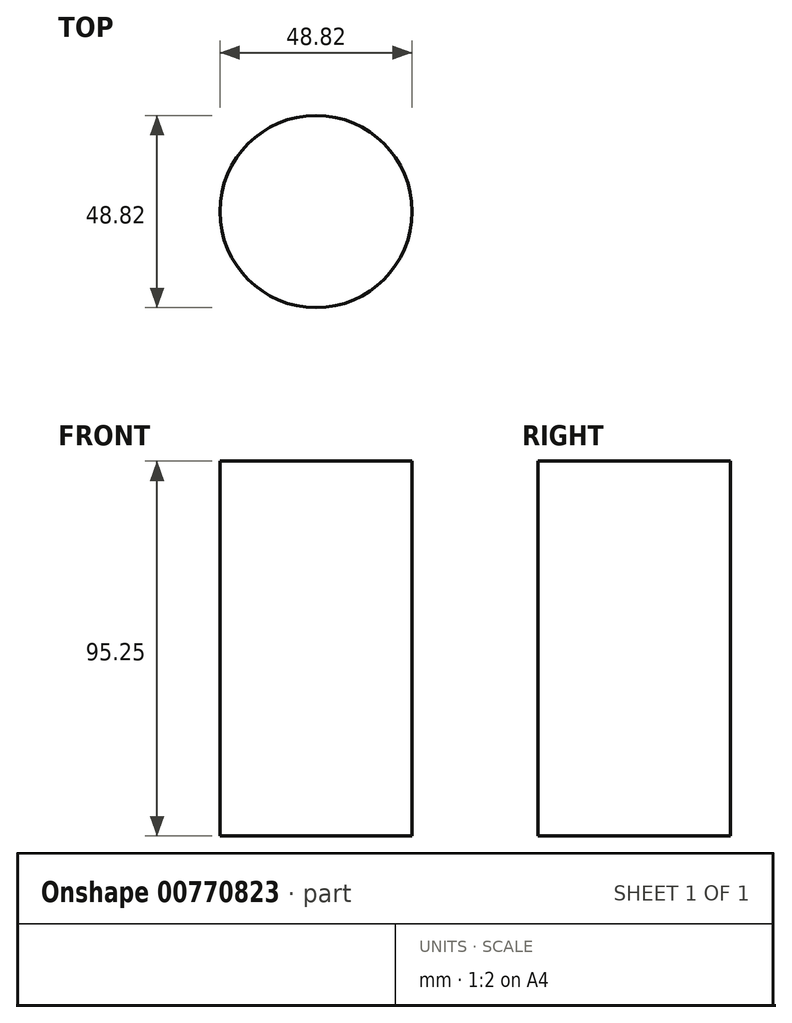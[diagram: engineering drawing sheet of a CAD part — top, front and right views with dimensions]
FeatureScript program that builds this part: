
annotation { "Feature Type Name" : "Feature", "Feature Type Description" : "" }
export const myFeature = defineFeature(function(context is Context, id is Id, definition is map)
    precondition{}
    {
        {
            var Q0;
            Q0=qCreatedBy(makeId("Top.planeOp"),FACE);
            var sketch = newSketch(context, id + "F0", { "sketchPlane" : qUnion([Q0])});
            skCircle(sketch, "E0", {"center": v(0, 0) * mm, "radius": 24.41 * mm});
            skSolve(sketch);
        }
        {
            var Q0;
            Q0=makeQuery(id+"F0.imprint","IMPRINT",FACE,{"disambiguationData":[TD([[makeQuery(id+"F0.imprint","IMPRINT",EDGE,{"derivedFrom":sQuery(id+"F0.wireOp",EDGE,"E0")}),1.0]])]});
            extrude(context, id + "F1", {"entities" : qUnion([Q0]), "depth" : 95.25 * mm, "offsetDistance" : 25.4 * mm});
        }
    });
